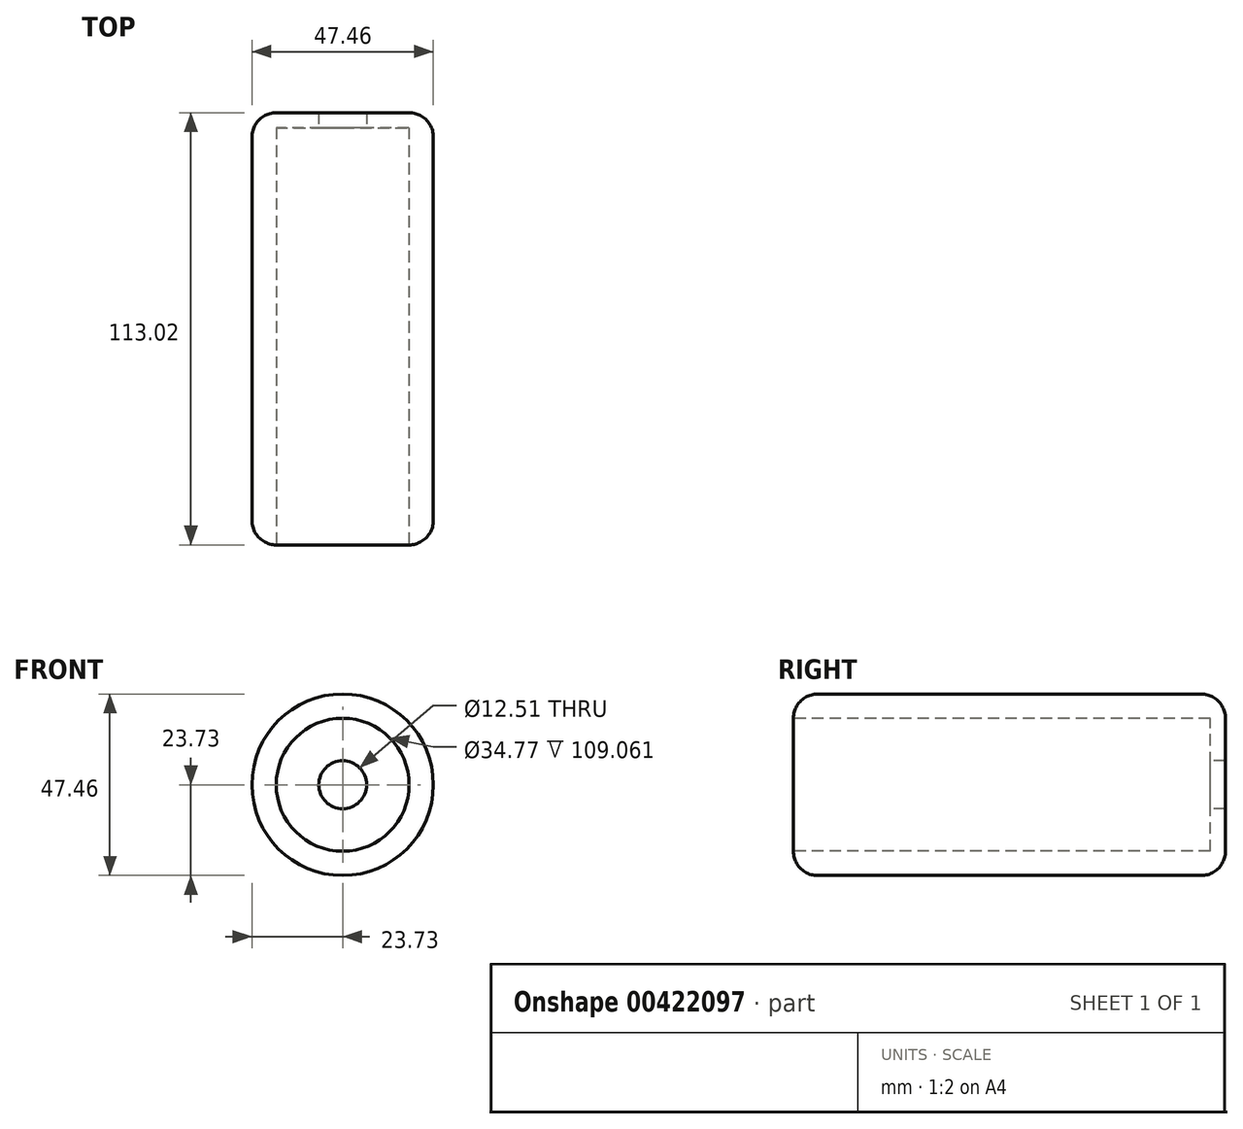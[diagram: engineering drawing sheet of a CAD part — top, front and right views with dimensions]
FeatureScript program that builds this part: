
annotation { "Feature Type Name" : "Feature", "Feature Type Description" : "" }
export const myFeature = defineFeature(function(context is Context, id is Id, definition is map)
    precondition{}
    {
        {
            var Q0;
            Q0=qCreatedBy(makeId("Right.planeOp"),FACE);
            var sketch = newSketch(context, id + "F0", { "sketchPlane" : qUnion([Q0])});
            skLineSegment(sketch, "E0", {"start": v(54.3, -23.73) * mm, "end": v(-59.2, -23.73) * mm});
            skLineSegment(sketch, "E1", {"start": v(54.3, -23.73) * mm, "end": v(54.3, -6.26) * mm});
            skLineSegment(sketch, "E2", {"start": v(54.3, -6.26) * mm, "end": v(50.35, -6.26) * mm});
            skLineSegment(sketch, "E3", {"start": v(50.35, -6.26) * mm, "end": v(50.35, -17.38) * mm});
            skLineSegment(sketch, "E4", {"start": v(50.35, -17.38) * mm, "end": v(-58.71, -17.38) * mm});
            skLineSegment(sketch, "E5", {"start": v(-58.71, -17.38) * mm, "end": v(-59.2, -23.73) * mm});
            skLineSegment(sketch, "E6", {"start": v(0, 0) * mm, "end": v(54.8, 0) * mm, "construction": true});
            skSolve(sketch);
        }
        {
            var Q0;
            Q0=makeQuery(id+"F0.imprint","IMPRINT",FACE,{"disambiguationData":[TD([[makeQuery(id+"F0.imprint","IMPRINT",EDGE,{"derivedFrom":sQuery(id+"F0.wireOp",EDGE,"E0")}),-1.0]])]});
            var Q1;
            Q1=sQuery(id+"F0.wireOp",EDGE,"E6");
            revolve(context, id + "F1", {"entities" : qUnion([Q0]), "axis" : qUnion([Q1]), "revolveType" : RevolveType.FULL});
        }
        {
            var Q0;
            Q0=makeQuery(id+"F1.opRevolve","SWEPT_EDGE",EDGE,{"disambiguationData":[OSD([sQuery(id+"F0.wireOp",EDGE,"E0"),sQuery(id+"F0.wireOp",EDGE,"E5")])]});
            var Q1;
            Q1=makeQuery(id+"F1.opRevolve","SWEPT_EDGE",EDGE,{"disambiguationData":[OSD([sQuery(id+"F0.wireOp",EDGE,"E0"),sQuery(id+"F0.wireOp",EDGE,"E1")])]});
            fillet(context, id + "F2", {"entities" : qUnion([Q0, Q1]), "radius" : 6.35 * mm, "tangentPropagation" : true, "allowEdgeOverflow" : false});
        }
    });
